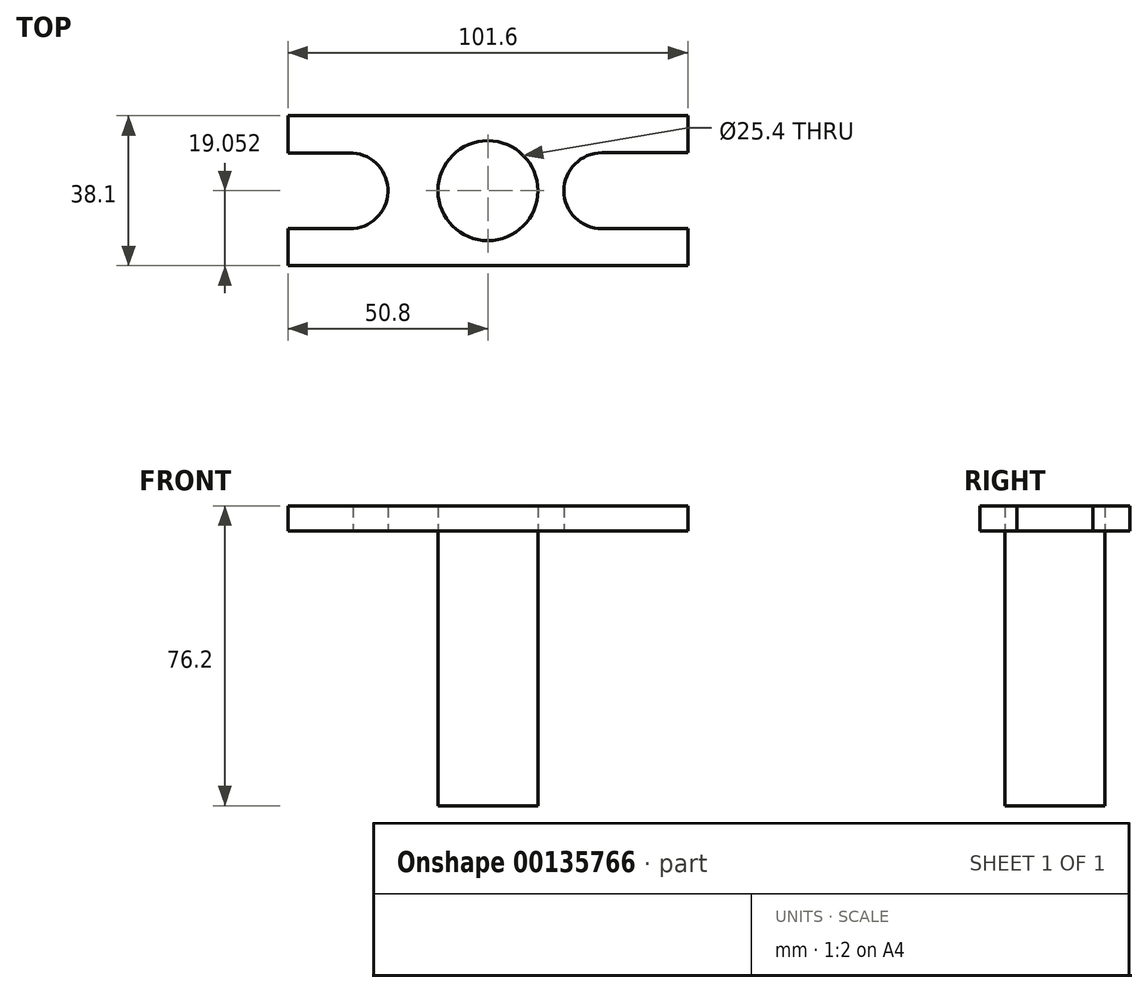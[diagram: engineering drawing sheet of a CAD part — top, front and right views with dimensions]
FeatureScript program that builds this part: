
annotation { "Feature Type Name" : "Feature", "Feature Type Description" : "" }
export const myFeature = defineFeature(function(context is Context, id is Id, definition is map)
    precondition{}
    {
        {
            var Q0;
            Q0=qCreatedBy(makeId("Top.planeOp"),FACE);
            var sketch = newSketch(context, id + "F0", { "sketchPlane" : qUnion([Q0])});
            skLineSegment(sketch, "E0", {"start": v(-50.8, 19.27) * mm, "end": v(-50.8, 28.7) * mm});
            skLineSegment(sketch, "E1", {"start": v(-50.8, 28.7) * mm, "end": v(50.8, 28.7) * mm});
            skLineSegment(sketch, "E2", {"start": v(50.8, 28.7) * mm, "end": v(50.8, 19.3) * mm});
            skLineSegment(sketch, "E3", {"start": v(-50.8, 19.27) * mm, "end": v(-34.3, 19.27) * mm});
            skLineSegment(sketch, "E4", {"start": v(50.8, 19.3) * mm, "end": v(28.98, 19.3) * mm});
            skLineSegment(sketch, "E5", {"start": v(-50.8, -9.4) * mm, "end": v(50.8, -9.4) * mm});
            skLineSegment(sketch, "E6", {"start": v(50.8, -9.4) * mm, "end": v(50.8, 0) * mm});
            skLineSegment(sketch, "E7", {"start": v(50.8, 0) * mm, "end": v(28.98, 0) * mm});
            skLineSegment(sketch, "E8", {"start": v(-50.8, -9.4) * mm, "end": v(-50.8, 0) * mm});
            skLineSegment(sketch, "E9", {"start": v(-50.8, 0) * mm, "end": v(-35.05, 0) * mm});
            skArc(sketch, "E10", {"start": v(-35.05, 0) * mm, "mid": v(-25.4, 9.27) * mm, "end": v(-34.3, 19.27) * mm});
            skArc(sketch, "E11", {"start": v(28.98, 19.3) * mm, "mid": v(19.33, 9.65) * mm, "end": v(28.98, 0) * mm});
            skLineSegment(sketch, "E12", {"start": v(-63.91, 9.65) * mm, "end": v(58.97, 9.65) * mm, "construction": true});
            skCircle(sketch, "E13", {"center": v(0, 9.65) * mm, "radius": 12.7 * mm});
            skSolve(sketch);
        }
        {
            var Q0;
            Q0 = qSketchRegion(id + "F0", true);
            extrude(context, id + "F1", {"entities" : qUnion([Q0]), "depth" : 6.35 * mm});
        }
        {
            var Q0;
            Q0=qCreatedBy(makeId("Top.planeOp"),FACE);
            var sketch = newSketch(context, id + "F2", { "sketchPlane" : qUnion([Q0])});
            skCircle(sketch, "E14", {"center": v(0, 9.65) * mm, "radius": 12.7 * mm});
            skSolve(sketch);
        }
        {
            var Q0;
            Q0 = qSketchRegion(id + "F2", true);
            extrude(context, id + "F3", {"entities" : qUnion([Q0]), "operationType" : NewBodyOperationType.ADD, "oppositeDirection" : true, "depth" : 69.85 * mm});
        }
    });
